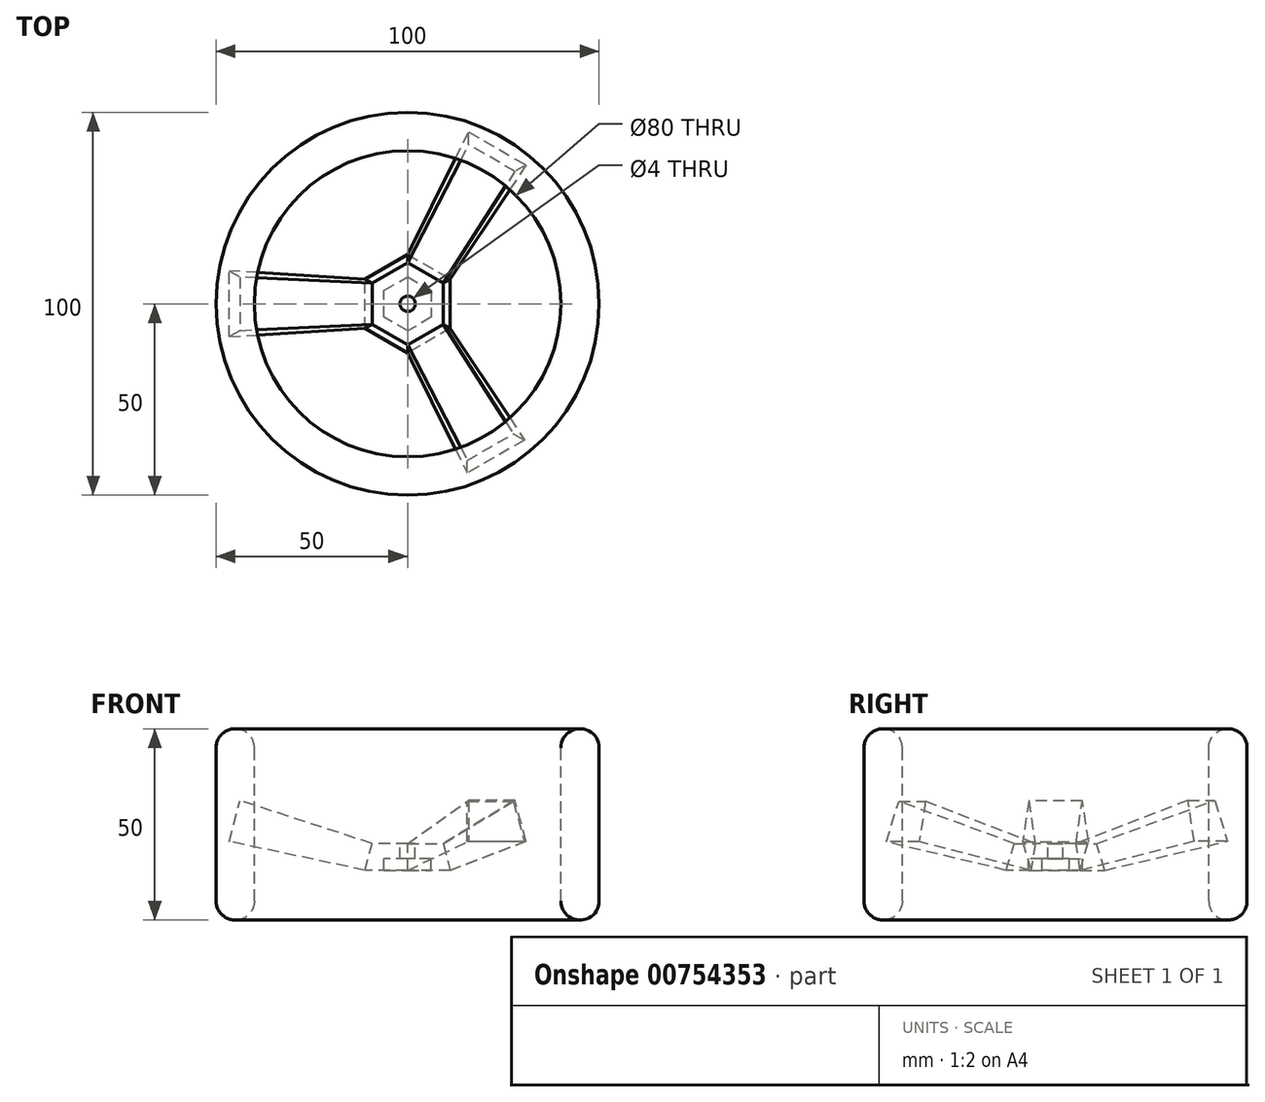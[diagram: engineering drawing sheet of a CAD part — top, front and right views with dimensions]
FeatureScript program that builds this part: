
annotation { "Feature Type Name" : "Feature", "Feature Type Description" : "" }
export const myFeature = defineFeature(function(context is Context, id is Id, definition is map)
    precondition{}
    {
        {
            var Q0;
            Q0=qCreatedBy(makeId("Top.planeOp"),FACE);
            var sketch = newSketch(context, id + "F0", { "sketchPlane" : qUnion([Q0])});
            skCircle(sketch, "E0.cCircle", {"center": v(0, 0) * mm, "radius": 6.13 * mm, "construction": true});
            skLineSegment(sketch, "E0.0", {"start": v(6.13, 3.54) * mm, "end": v(6.13, -3.54) * mm});
            skLineSegment(sketch, "E0.1", {"start": v(6.13, -3.54) * mm, "end": v(0, -7.08) * mm});
            skLineSegment(sketch, "E0.2", {"start": v(0, -7.08) * mm, "end": v(-6.14, -3.54) * mm});
            skLineSegment(sketch, "E0.3", {"start": v(-6.13, -3.54) * mm, "end": v(-6.13, 3.54) * mm});
            skLineSegment(sketch, "E0.4", {"start": v(-6.13, 3.54) * mm, "end": v(0, 7.08) * mm});
            skLineSegment(sketch, "E0.5", {"start": v(0, 7.08) * mm, "end": v(6.14, 3.54) * mm});
            skPoint(sketch, "E0.0.midPoint", {"position": v(6.13, 0) * mm});
            skCircle(sketch, "E1.cCircle", {"center": v(0, 0) * mm, "radius": 11.13 * mm, "construction": true});
            skLineSegment(sketch, "E1.0", {"start": v(11.13, 6.43) * mm, "end": v(11.13, -6.43) * mm});
            skLineSegment(sketch, "E1.1", {"start": v(11.14, -6.43) * mm, "end": v(0, -12.86) * mm});
            skLineSegment(sketch, "E1.2", {"start": v(0, -12.86) * mm, "end": v(-11.14, -6.43) * mm});
            skLineSegment(sketch, "E1.3", {"start": v(-11.13, -6.43) * mm, "end": v(-11.13, 6.43) * mm});
            skLineSegment(sketch, "E1.4", {"start": v(-11.13, 6.43) * mm, "end": v(0, 12.86) * mm});
            skLineSegment(sketch, "E1.5", {"start": v(0, 12.86) * mm, "end": v(11.14, 6.43) * mm});
            skPoint(sketch, "E1.0.midPoint", {"position": v(11.13, 0) * mm});
            skCircle(sketch, "E2", {"center": v(0, 0) * mm, "radius": 45 * mm});
            skCircle(sketch, "E3", {"center": v(0, 0) * mm, "radius": 2 * mm});
            skCircle(sketch, "E4", {"center": v(0, 0) * mm, "radius": 5.05 * mm});
            skSolve(sketch);
        }
        {
            var Q0;
            Q0=qCreatedBy(makeId("Top.planeOp"),FACE);
            cPlane(context, id + "F1", {"entities" : qUnion([Q0]), "cplaneType" : CPlaneType.OFFSET, "offset" : 30 * mm, "width" : 150 * mm, "height" : 150 * mm});
        }
        {
            var Q0;
            Q0=qCreatedBy(id+"F1.planeOp",FACE);
            var sketch = newSketch(context, id + "F2", { "sketchPlane" : qUnion([Q0])});
            skCircle(sketch, "E5", {"center": v(0, 0) * mm, "radius": 50 * mm});
            skCircle(sketch, "E6", {"center": v(0, 0) * mm, "radius": 40 * mm});
            skSolve(sketch);
        }
        {
            var Q0;
            Q0=makeQuery(id+"F2.imprint","IMPRINT",FACE,{"disambiguationData":[TD([[makeQuery(id+"F2.imprint","IMPRINT",EDGE,{"derivedFrom":sQuery(id+"F2.wireOp",EDGE,"E5")}),1.0]])]});
            extrude(context, id + "F3", {"entities" : qUnion([Q0]), "oppositeDirection" : true, "depth" : 50 * mm, "offsetDistance" : 25 * mm});
        }
        {
            var Q0;
            Q0=makeQuery(id+"F0.imprint","IMPRINT",FACE,{"disambiguationData":[TD([[makeQuery(id+"F0.imprint","IMPRINT",EDGE,{"derivedFrom":sQuery(id+"F0.wireOp",EDGE,"E0.0")}),-1.0]])]});
            extrude(context, id + "F4", {"entities" : qUnion([Q0]), "oppositeDirection" : true, "depth" : 4 * mm, "offsetDistance" : 25 * mm});
        }
        {
            var Q0;
            Q0=makeQuery(id+"F0.imprint","IMPRINT",FACE,{"disambiguationData":[TD([[makeQuery(id+"F0.imprint","IMPRINT",EDGE,{"derivedFrom":sQuery(id+"F0.wireOp",EDGE,"E0.0")}),1.0]])]});
            extrude(context, id + "F5", {"entities" : qUnion([Q0]), "operationType" : NewBodyOperationType.ADD, "oppositeDirection" : true, "depth" : 7 * mm, "offsetDistance" : 25 * mm});
        }
        {
            var Q0;
            Q0=makeQuery(id+"F0.imprint","IMPRINT",FACE,{"disambiguationData":[TD([[makeQuery(id+"F0.imprint","IMPRINT",EDGE,{"derivedFrom":sQuery(id+"F0.wireOp",EDGE,"E3")}),1.0]])]});
            extrude(context, id + "F6", {"entities" : qUnion([Q0]), "operationType" : NewBodyOperationType.REMOVE, "depth" : 58.6 * mm, "offsetDistance" : 25 * mm});
        }
        {
            var Q0;
            Q0=makeQuery(id+"F3.opExtrude","CAP_EDGE",EDGE,{"disambiguationData":[OSD([sQuery(id+"F2.wireOp",EDGE,"E6")])],"isStart":false});
            var Q1;
            Q1=makeQuery(id+"F3.opExtrude","CAP_EDGE",EDGE,{"disambiguationData":[OSD([sQuery(id+"F2.wireOp",EDGE,"E5")])],"isStart":false});
            fillet(context, id + "F7", {"entities" : qUnion([Q0, Q1]), "radius" : 5 * mm, "tangentPropagation" : true, "allowEdgeOverflow" : false});
        }
        {
            var Q0;
            Q0=makeQuery(id+"F3.opExtrude","CAP_EDGE",EDGE,{"disambiguationData":[OSD([sQuery(id+"F2.wireOp",EDGE,"E6")])],"isStart":true});
            var Q1;
            Q1=makeQuery(id+"F3.opExtrude","CAP_EDGE",EDGE,{"disambiguationData":[OSD([sQuery(id+"F2.wireOp",EDGE,"E5")])],"isStart":true});
            fillet(context, id + "F8", {"entities" : qUnion([Q0, Q1]), "radius" : 5 * mm, "tangentPropagation" : true, "allowEdgeOverflow" : false});
        }
        {
            var Q0;
            Q0=makeQuery(id+"F0.imprint","IMPRINT",FACE,{"disambiguationData":[TD([[makeQuery(id+"F0.imprint","IMPRINT",EDGE,{"derivedFrom":sQuery(id+"F0.wireOp",EDGE,"E3")}),-1.0]])]});
            extrude(context, id + "F9", {"entities" : qUnion([Q0]), "operationType" : NewBodyOperationType.ADD, "oppositeDirection" : true, "depth" : 4 * mm, "offsetDistance" : 25 * mm});
        }
        {
            var Q0;
            Q0=makeQuery(id+"F5.opExtrude","CAP_EDGE",EDGE,{"disambiguationData":[OSD([sQuery(id+"F0.wireOp",EDGE,"E1.2")])],"isStart":true});
            var Q1;
            Q1=makeQuery(id+"F5.opExtrude","CAP_EDGE",EDGE,{"disambiguationData":[OSD([sQuery(id+"F0.wireOp",EDGE,"E1.5")])],"isStart":true});
            var Q2;
            Q2=makeQuery(id+"F5.opExtrude","CAP_EDGE",EDGE,{"disambiguationData":[OSD([sQuery(id+"F0.wireOp",EDGE,"E1.0")])],"isStart":true});
            var Q3;
            Q3=makeQuery(id+"F5.opExtrude","CAP_EDGE",EDGE,{"disambiguationData":[OSD([sQuery(id+"F0.wireOp",EDGE,"E1.3")])],"isStart":true});
            var Q4;
            Q4=makeQuery(id+"F5.opExtrude","CAP_EDGE",EDGE,{"disambiguationData":[OSD([sQuery(id+"F0.wireOp",EDGE,"E1.4")])],"isStart":true});
            var Q5;
            Q5=makeQuery(id+"F5.opExtrude","CAP_EDGE",EDGE,{"disambiguationData":[OSD([sQuery(id+"F0.wireOp",EDGE,"E1.1")])],"isStart":true});
            chamfer(context, id + "F10", {"entities" : qUnion([Q0, Q1, Q2, Q3, Q4, Q5]), "chamferType" : ChamferType.OFFSET_ANGLE, "width" : 7 * mm, "oppositeDirection" : false, "angle" : 15 * degree, "tangentPropagation" : true});
        }
        {
            var Q0;
            Q0=makeQuery(id+"F10.opChamfer","BLEND_FACE",FACE,{"disambiguationData":[OSD([sQuery(id+"F0.wireOp",EDGE,"E1.5")])]});
            extrude(context, id + "F11", {"entities" : qUnion([Q0]), "depth" : 36.42 * mm, "offsetDistance" : 25 * mm, "hasDraft" : true, "draftAngle" : 3 * degree});
        }
        {
            var Q0;
            Q0=makeQuery(id+"F10.opChamfer","BLEND_FACE",FACE,{"disambiguationData":[OSD([sQuery(id+"F0.wireOp",EDGE,"E1.1")])]});
            extrude(context, id + "F12", {"entities" : qUnion([Q0]), "depth" : 35.65 * mm, "offsetDistance" : 25 * mm, "hasDraft" : true, "draftAngle" : 3 * degree});
        }
        {
            var Q0;
            Q0=makeQuery(id+"F10.opChamfer","BLEND_FACE",FACE,{"disambiguationData":[OSD([sQuery(id+"F0.wireOp",EDGE,"E1.3")])]});
            extrude(context, id + "F13", {"entities" : qUnion([Q0]), "depth" : 36.22 * mm, "offsetDistance" : 25 * mm, "hasDraft" : true, "draftAngle" : 3 * degree});
        }
    });
